# Revit family: 01-82-001-DN50-100
name_source: partatom
category: Pipe Accessories
units: mm (PartAtom-declared; Revit-internal decimal feet)

## family parameters
Always vertical = No
Cut with Voids When Loaded = No
Part Type = Valve - Breaks Into
Round Connector Dimension = Use Diameter
Shared = No
Work Plane-Based = No

## types (3) — shared parameters
2 = 2 mm  [stored 0.00656168 ft]
DN050_PN16 = 01-060-82-0140099
DN075_PN16 = 01-085-82-0140099
DN100_PN16 = 01-110-82-0140099
Description_ = AVK SOCKET END GATE VALVE, 16 BAR
Search_table = 01-82-001 DN50-100
Thickness = 9 mm  [stored 0.0295276 ft]
URL product pages = https://www.avkvalves.com
zero-valued in all types: Bonnet_FL_T, Default Elevation

## per-type parameters (varying)
- DN050_PN16: Body_H=140 mm; Body_dim1=61 mm; Body_dim2=30 mm  [stored 0.0984252 ft]; Bolt=13 mm; Bolt_T=7 mm  [stored 0.0229659 ft]; Bonne_end=244 mm; Bonnet_Bolt1=9 mm  [stored 0.0295276 ft]; Bonnet_Bolt2=14 mm  [stored 0.0459318 ft]; Bonnet_W=56 mm; Bonnet_dim1=39 mm  [stored 0.127953 ft]; Bonnet_dim2=8 mm  [stored 0.0262467 ft]; Bonnet_dim3=42 mm  [stored 0.137795 ft]; Bonnet_dim4=23 mm; Bonnet_dim5=19 mm  [stored 0.062336 ft]; Bonnet_dim6=17 mm  [stored 0.0557743 ft]; Bore=25 mm  [stored 0.082021 ft]; DN=50 mm  [stored 0.164042 ft]; Dd=60 mm  [stored 0.19685 ft]; EPDM=58 mm  [stored 0.190289 ft]; F1=14 mm  [stored 0.0459318 ft]; Fillet=15 mm  [stored 0.0492126 ft]; H=52 mm; H3=271 mm; L=200 mm; Location1=176 mm; Location2=50 mm  [stored 0.164042 ft]; Rib_dim1=30 mm  [stored 0.0984252 ft]; Rib_dim2=24 mm  [stored 0.0787402 ft]; W=135 mm; W_actual=68 mm
- DN075_PN16: Body_H=184 mm; Body_dim1=78 mm; Body_dim2=35 mm; Bolt=15 mm  [stored 0.0492126 ft]; Bolt_T=9 mm  [stored 0.0295276 ft]; Bonne_end=323 mm; Bonnet_Bolt1=11 mm  [stored 0.0360892 ft]; Bonnet_Bolt2=16 mm; Bonnet_W=72 mm; Bonnet_dim1=45 mm; Bonnet_dim2=9 mm  [stored 0.0295276 ft]; Bonnet_dim3=51 mm; Bonnet_dim4=27 mm  [stored 0.0885827 ft]; Bonnet_dim5=22 mm; Bonnet_dim6=20 mm  [stored 0.0656168 ft]; Bore=38 mm; DN=75 mm; Dd=85 mm; EPDM=83 mm; F1=17 mm  [stored 0.0557743 ft]; Fillet=18 mm  [stored 0.0590551 ft]; H=68 mm; H3=359 mm; L=232 mm; Location1=204 mm; Location2=58 mm  [stored 0.190289 ft]; Rib_dim1=38 mm; Rib_dim2=31 mm; W=173 mm; W_actual=87 mm
- DN100_PN16: Body_H=216 mm; Body_dim1=86 mm; Body_dim2=38 mm; Bolt=17 mm  [stored 0.0557743 ft]; Bolt_T=10 mm  [stored 0.0328084 ft]; Bonne_end=355 mm; Bonnet_Bolt1=12 mm  [stored 0.0393701 ft]; Bonnet_Bolt2=18 mm  [stored 0.0590551 ft]; Bonnet_W=80 mm; Bonnet_dim1=49 mm; Bonnet_dim2=10 mm  [stored 0.0328084 ft]; Bonnet_dim3=57 mm  [stored 0.187008 ft]; Bonnet_dim4=29 mm  [stored 0.0951444 ft]; Bonnet_dim5=23 mm; Bonnet_dim6=21 mm; Bore=50 mm  [stored 0.164042 ft]; DN=100 mm; Dd=110 mm; EPDM=108 mm; F1=19 mm  [stored 0.062336 ft]; Fillet=20 mm  [stored 0.0656168 ft]; H=80 mm; H3=394 mm; L=250 mm; Location1=220 mm; Location2=63 mm; Rib_dim1=43 mm; Rib_dim2=34 mm; W=192 mm; W_actual=96 mm

note: [stored X ft] marks values corroborated as IEEE doubles in the binary element streams (Revit-internal decimal feet)

## geometry (parser evidence)
native form markers: Sweep x6
no freeform markers — native parametric forms only
